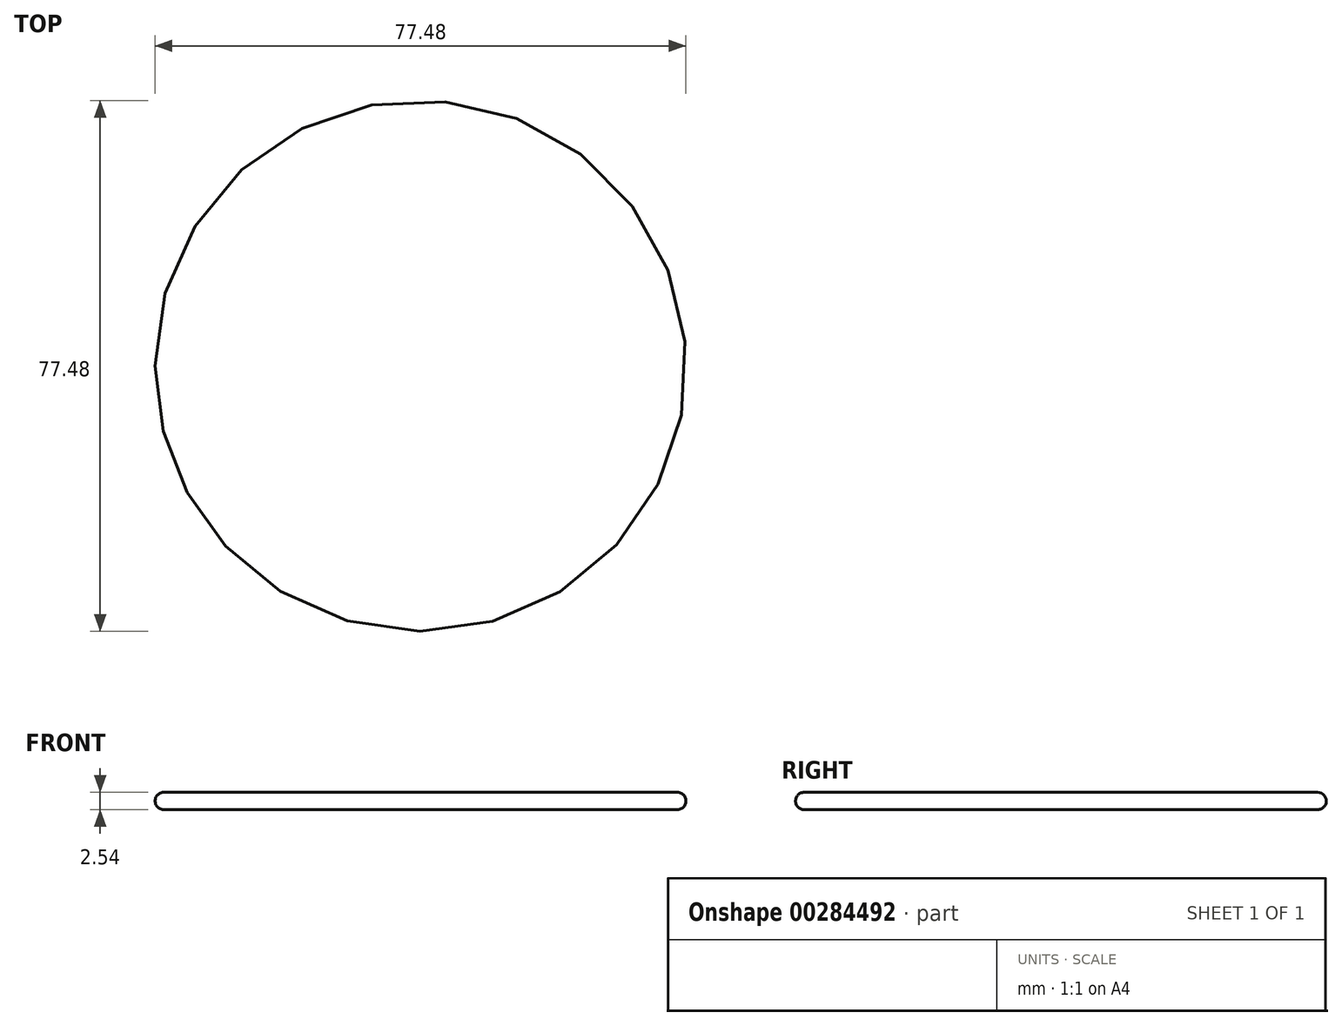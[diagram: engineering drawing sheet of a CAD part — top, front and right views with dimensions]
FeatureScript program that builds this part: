
annotation { "Feature Type Name" : "Feature", "Feature Type Description" : "" }
export const myFeature = defineFeature(function(context is Context, id is Id, definition is map)
    precondition{}
    {
        {
            var Q0;
            Q0=qCreatedBy(makeId("Front.planeOp"),FACE);
            var sketch = newSketch(context, id + "F0", { "sketchPlane" : qUnion([Q0])});
            skLineSegment(sketch, "E0", {"start": v(0, 0) * mm, "end": v(0, 109.3) * mm, "construction": true});
            skLineSegment(sketch, "E1", {"start": v(0, 0) * mm, "end": v(-37.47, 0) * mm});
            skLineSegment(sketch, "E2.0", {"start": v(0, 2.54) * mm, "end": v(-37.47, 2.54) * mm});
            skArc(sketch, "E3", {"start": v(-37.47, 2.54) * mm, "mid": v(-38.74, 1.27) * mm, "end": v(-37.47, 0) * mm});
            skLineSegment(sketch, "E4", {"start": v(0, 2.54) * mm, "end": v(0, 0) * mm});
            skSolve(sketch);
        }
        {
            var Q0;
            Q0=makeQuery(id+"F0.imprint","IMPRINT",FACE,{"disambiguationData":[TD([[makeQuery(id+"F0.imprint","IMPRINT",EDGE,{"derivedFrom":sQuery(id+"F0.wireOp",EDGE,"E1")}),-1.0]])]});
            var Q1;
            Q1=sQuery(id+"F0.wireOp",EDGE,"E0");
            revolve(context, id + "F1", {"entities" : qUnion([Q0]), "axis" : qUnion([Q1]), "revolveType" : RevolveType.FULL});
        }
    });
